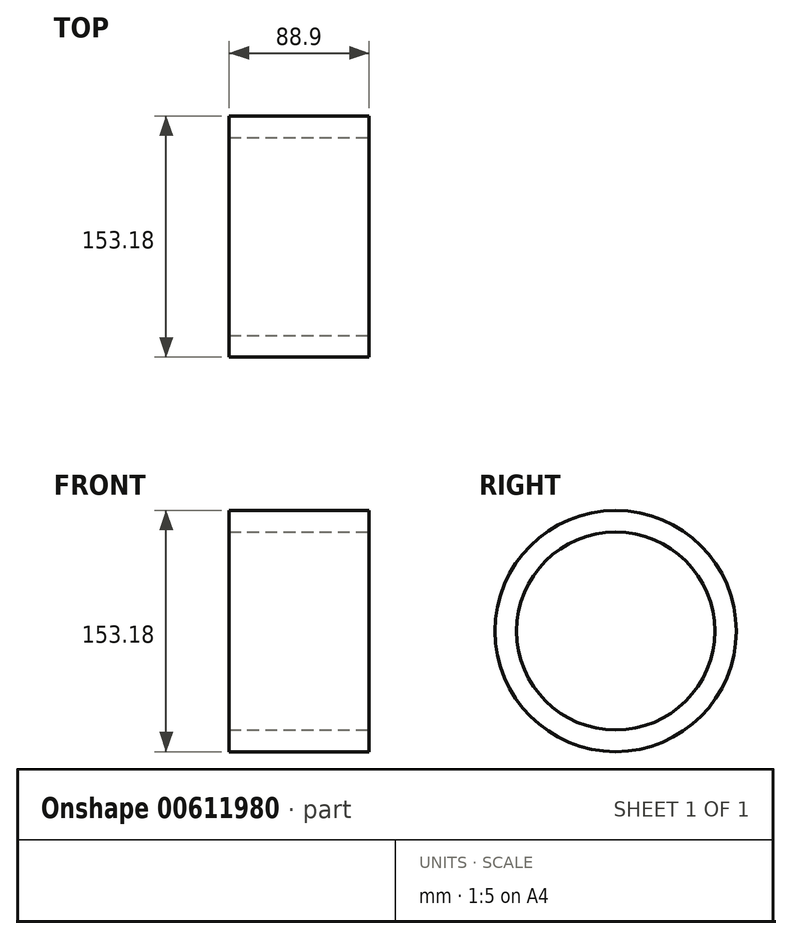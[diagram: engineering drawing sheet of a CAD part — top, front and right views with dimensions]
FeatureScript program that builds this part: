
annotation { "Feature Type Name" : "Feature", "Feature Type Description" : "" }
export const myFeature = defineFeature(function(context is Context, id is Id, definition is map)
    precondition{}
    {
        {
            var Q0;
            Q0=qCreatedBy(makeId("Right.planeOp"),FACE);
            var sketch = newSketch(context, id + "F0", { "sketchPlane" : qUnion([Q0])});
            skCircle(sketch, "E0", {"center": v(0, 0) * mm, "radius": 76.59 * mm});
            skCircle(sketch, "E1", {"center": v(0, 0) * mm, "radius": 62.9 * mm});
            skSolve(sketch);
        }
        {
            var Q0;
            Q0=sQuery(id+"F0.wireOp",EDGE,"E1");
            var Q1;
            Q1=sQuery(id+"F0.wireOp",EDGE,"E0");
            extrude(context, id + "F1", {"bodyType" : ToolBodyType.SURFACE, "surfaceEntities" : qUnion([Q0, Q1]), "depth" : 88.9 * mm, "offsetDistance" : 25.4 * mm});
        }
    });
